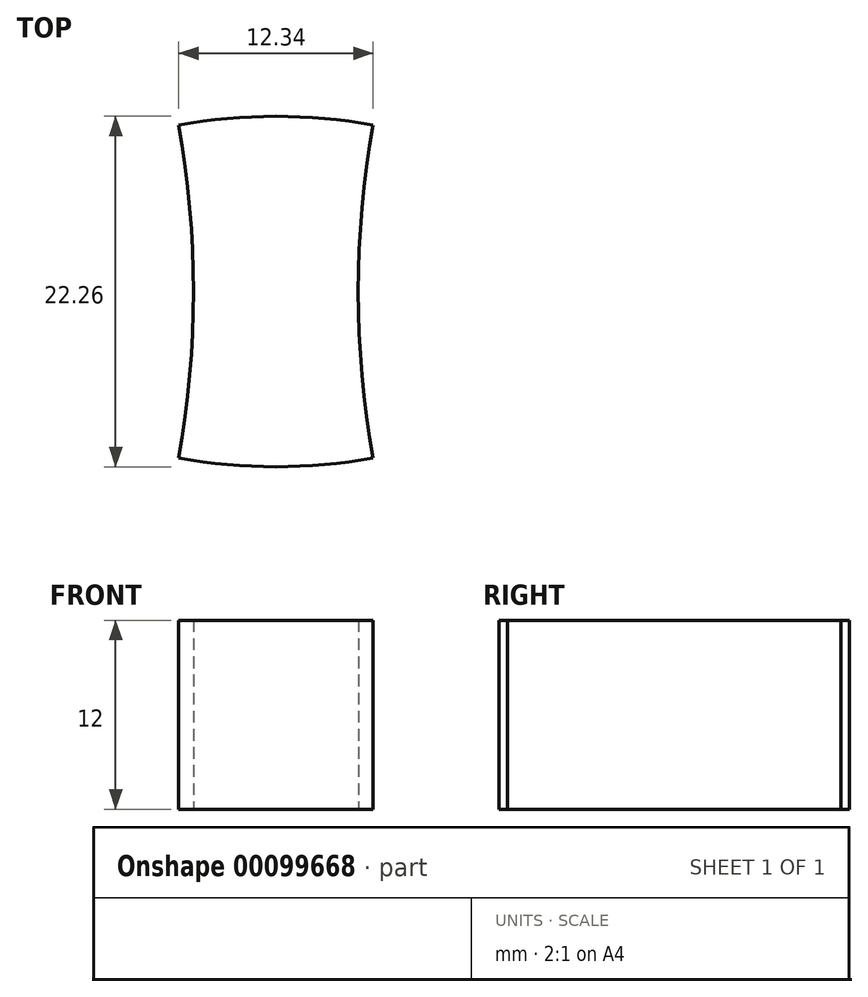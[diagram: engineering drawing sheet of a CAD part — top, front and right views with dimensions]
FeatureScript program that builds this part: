
annotation { "Feature Type Name" : "Feature", "Feature Type Description" : "" }
export const myFeature = defineFeature(function(context is Context, id is Id, definition is map)
    precondition{}
    {
        {
            var Q0;
            Q0=qCreatedBy(makeId("Top.planeOp"),FACE);
            var sketch = newSketch(context, id + "F0", { "sketchPlane" : qUnion([Q0])});
            skArc(sketch, "E0", {"start": v(0, 22.26) * mm, "mid": v(-3.1, 22.12) * mm, "end": v(-6.17, 21.71) * mm});
            skArc(sketch, "E1", {"start": v(-6.17, 0.55) * mm, "mid": v(-3.1, 0.14) * mm, "end": v(0, 0) * mm});
            skLineSegment(sketch, "E2", {"start": v(0, 0) * mm, "end": v(0, 22.26) * mm});
            skLineSegment(sketch, "E3", {"start": v(0, 11.13) * mm, "end": v(-47.46, 11.13) * mm, "construction": true});
            skArc(sketch, "E4", {"start": v(-6.17, 0.55) * mm, "mid": v(-5.23, 11.13) * mm, "end": v(-6.17, 21.71) * mm});
            skLineSegment(sketch, "E5", {"start": v(-6.17, 21.71) * mm, "end": v(-3.5, 22.19) * mm, "construction": true});
            skLineSegment(sketch, "E6", {"start": v(-6.17, 21.71) * mm, "end": v(-7.03, 26.5) * mm, "construction": true});
            skLineSegment(sketch, "E7", {"start": v(-6.17, 0.55) * mm, "end": v(-7.64, -7.63) * mm, "construction": true});
            skLineSegment(sketch, "E8", {"start": v(-6.17, 0.55) * mm, "end": v(1.99, -0.91) * mm, "construction": true});
            skSolve(sketch);
        }
        {
            var Q0;
            Q0=makeQuery(id+"F0.imprint","IMPRINT",FACE,{"disambiguationData":[TD([[makeQuery(id+"F0.imprint","IMPRINT",EDGE,{"derivedFrom":sQuery(id+"F0.wireOp",EDGE,"E0")}),1.0]])]});
            extrude(context, id + "F1", {"entities" : qUnion([Q0]), "depth" : 12 * mm});
        }
        {
            var Q0;
            Q0=makeQuery(id+"F1.opExtrude","SWEPT_BODY",BODY,{"disambiguationData":[OSD([sQuery(id+"F0.wireOp",EDGE,"E0"),sQuery(id+"F0.wireOp",EDGE,"E1"),sQuery(id+"F0.wireOp",EDGE,"E2"),sQuery(id+"F0.wireOp",EDGE,"E4")])]});
            var Q1;
            Q1=qCreatedBy(makeId("Right.planeOp"),FACE);
            mirror(context, id + "F2", {"operationType" : NewBodyOperationType.ADD, "entities" : qUnion([Q0]), "mirrorPlane" : qUnion([Q1])});
        }
    });
